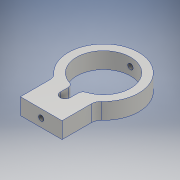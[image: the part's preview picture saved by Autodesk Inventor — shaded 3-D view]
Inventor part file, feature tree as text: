
AUTODESK INVENTOR PART (.ipt)
format: ipt  version: 2017 SP1 (Build 210196100, 196)  size: 160,256 bytes
history: native  units: mm
features: sketch x3, extrude x2, fillet x2, hole x2, plane x2
ambient origin geometry x8: Origin, YZ Plane, XZ Plane, XY Plane, X Axis, Y Axis, Z Axis, Center Point
bodies: Solid1 (feature_tree)
feature tree (11):
  extrude  "Extrusion1"  Depth=33.0mm
  fillet  "Fillet2"  Radius=43.0mm
  hole  "Hole1"  [1 undecoded]
  plane  "Work Plane1"
  hole  "Hole2"  [1 undecoded]
  extrude  "Extrusion3"  Depth=6.0mm
  fillet  "Fillet4"  [1 undecoded]
  plane  "Work Plane2"
  sketch  "Sketch1"  dims[d0=30.0mm d1=33.0mm d2=43.0mm]
  sketch  "Sketch3"  dims[d4=10.0mm d5=0.0mm d7=25.4mm]
  sketch  "Sketch4"  dims[d8=38.1mm d9=6.0mm d14=3.242mm d15=8.0mm d16=4.0mm d17=2.0mm d18=90.0deg d19=10.0mm d20=20.594885mm d21=3.302mm d22=8.331mm d23=4.0mm d24=2.0mm d25=90.0deg d26=12.3mm d27=20.594885mm d28=6.0mm d29=0.0mm d30=0.0mm d31=3.0mm d32=10.0mm]
note: 3 required parameter values undecoded (feature->parameter linkage not recoverable at this tier; creation-order binding heuristic only, values carry confidence <= 0.55)
